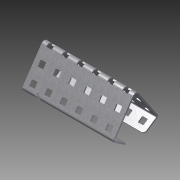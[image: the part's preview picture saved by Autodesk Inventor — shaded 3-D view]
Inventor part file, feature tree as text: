
AUTODESK INVENTOR PART (.ipt)
format: ipt  version: 2012 (Build 160160000, 160)  size: 2,086,912 bytes
history: native  units: in
note: dims shown in document units (in); Inventor stores cm internally (conversion verified against a paired STEP export)
features: sketch x8, other x6, imported_body x1, plane x1, split x1
ambient origin geometry x8: Origin, YZ Plane, XZ Plane, XY Plane, X Axis, Y Axis, Z Axis, Center Point
feature tree (17):
  parser-record x1  (decoder bookkeeping rows leaked as tree rows — omitted from the tree; the rows remain in map.json)
  imported_body  "Base1"
  sketch  "Sketch1"  dims[d0=5.9055in d2=0.5in d3=0.3937in d5=1.0in]
  sketch  "Sketch2"  dims[d7=5.9055in d9=0.5in d10=1.9685in d12=0.5in]
  sketch  "Sketch3"  dims[d15=0.5in]
  plane  "Work Plane1"
  split  "Split1"
  other  "Bend Part1"
  sketch  "Sketch5"  dims[d20=0.07in d21=0.7696in]
  sketch  "Sketch6"
  other  "Work Point1"
  other  "Work Point2"
  sketch  "Sketch7"
  sketch  "Sketch8"
  other  "Work Point3"
  other  "Work Point4"
  sketch  "Sketch4"  dims[d19=-3.0in]
